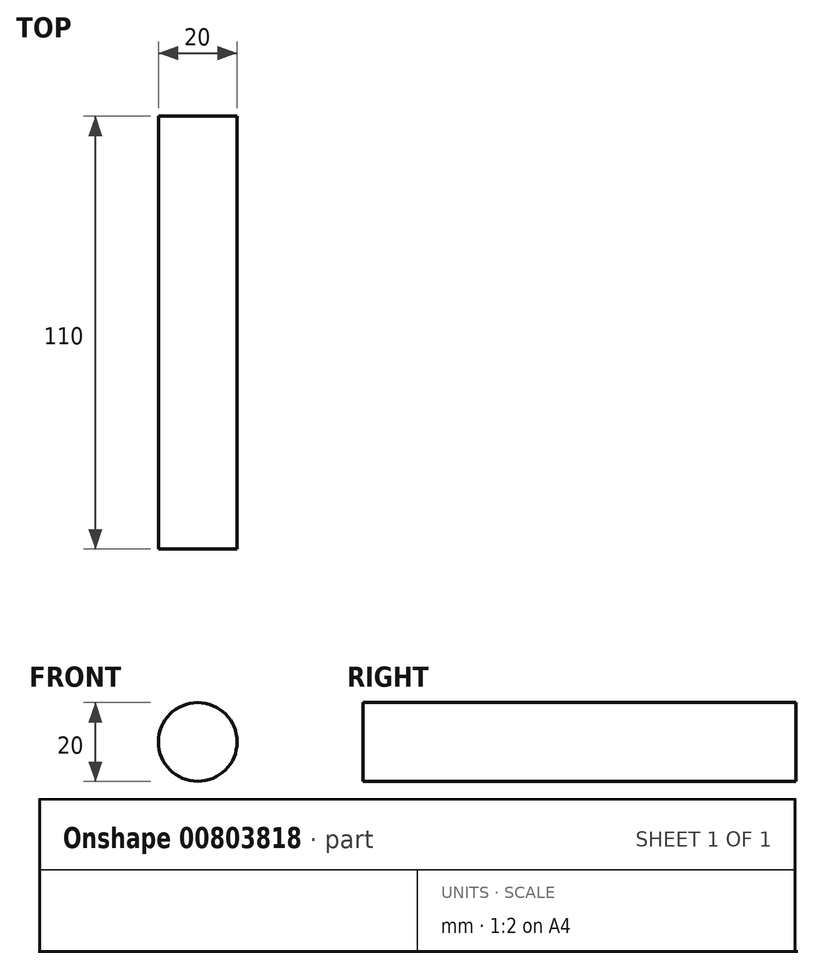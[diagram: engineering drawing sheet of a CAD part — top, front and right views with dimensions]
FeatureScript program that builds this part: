
annotation { "Feature Type Name" : "Feature", "Feature Type Description" : "" }
export const myFeature = defineFeature(function(context is Context, id is Id, definition is map)
    precondition{}
    {
        {
            var Q0;
            Q0=qCreatedBy(makeId("Front.planeOp"),FACE);
            var sketch = newSketch(context, id + "F0", { "sketchPlane" : qUnion([Q0])});
            skCircle(sketch, "E0", {"center": v(0, 0) * mm, "radius": 10 * mm});
            skSolve(sketch);
        }
        {
            var Q0;
            Q0=makeQuery(id+"F0.imprint","IMPRINT",FACE,{"disambiguationData":[TD([[makeQuery(id+"F0.imprint","IMPRINT",EDGE,{"derivedFrom":sQuery(id+"F0.wireOp",EDGE,"E0")}),1.0]])]});
            extrude(context, id + "F1", {"entities" : qUnion([Q0]), "depth" : 110 * mm, "offsetDistance" : 25 * mm});
        }
    });
